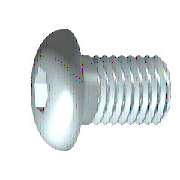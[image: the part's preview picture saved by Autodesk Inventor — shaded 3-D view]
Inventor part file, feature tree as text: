
AUTODESK INVENTOR PART (.ipt)
format: ipt  version: 2023.5 (Build 275446000, 446)  size: 198,656 bytes
history: native  units: mm (DEFAULTED — no unit token found)
features: extrude x1, plane x1, fillet x1
ambient origin geometry x7: Origin, YZ Plane, XY Plane, X Axis, Y Axis, Z Axis, Center Point
bodies: Solid1 (feature_tree), Body (feature_tree)
feature tree (3):
  extrude  "Slot"  Depth=7.937246mm
  plane  "Work Plane1"
  fillet  "Fillet2"  Radius=1.5876mm
